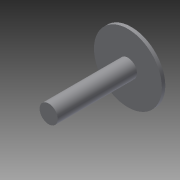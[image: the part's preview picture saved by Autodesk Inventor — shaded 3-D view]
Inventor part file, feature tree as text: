
AUTODESK INVENTOR PART (.ipt)
format: ipt  version: 2013 (Build 170138000, 138)  size: 81,408 bytes
history: native  units: mm
features: extrude x3, sketch x3, other x1
ambient origin geometry x8: Origin, YZ Plane, XZ Plane, XY Plane, X Axis, Y Axis, Z Axis, Center Point
feature tree (7):
  other  "ソリッド1"
  extrude  "押し出し1"  Depth=16.0mm
  sketch  "スケッチ2"
  extrude  "押し出し2"  Depth=70.0mm TaperAngle=0.0deg
  extrude  "押し出し3"  Depth=60.0mm
  sketch  "スケッチ1"
  sketch  "スケッチ3"
